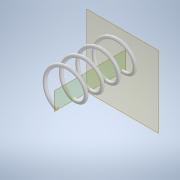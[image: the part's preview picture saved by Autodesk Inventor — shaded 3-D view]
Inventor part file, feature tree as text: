
AUTODESK INVENTOR PART (.ipt)
format: ipt  version: 2021 (Build 250183000, 183)  size: 431,104 bytes
history: native  units: mm
features: other x7, reference x7, sketch x2, sweep x1
ambient origin geometry x8: Origin, YZ Plane, XZ Plane, XY Plane, X Axis, Y Axis, Z Axis, Center Point
bodies: Body1 (feature_tree)
feature tree (17):
  other  "Bryła1"
  sketch  "Szkic 3D1"
  other  "Płaszczyzna konstrukcyjna1"
  other  "Płaszczyzna konstrukcyjna2"
  sweep  "Przeciągnięcie1"
  other  "Krzywa śrubowa1"
  sketch  "Szkic1"
  reference  "Odniesienie1"
  reference  "Odniesienie2"
  reference  "Odniesienie3"
  reference  "Odniesienie4"
  reference  "Odniesienie5"
  reference  "Odniesienie6"
  reference  "Odniesienie7"
  parser-record x1  (decoder bookkeeping rows leaked as tree rows — omitted from the tree; the rows remain in map.json)
  other  "zespoluchwyt.iam"
  other  "uchwyt1:1"
note: 1 file-system path scrubbed to <path> (originals preserved in map.json)
